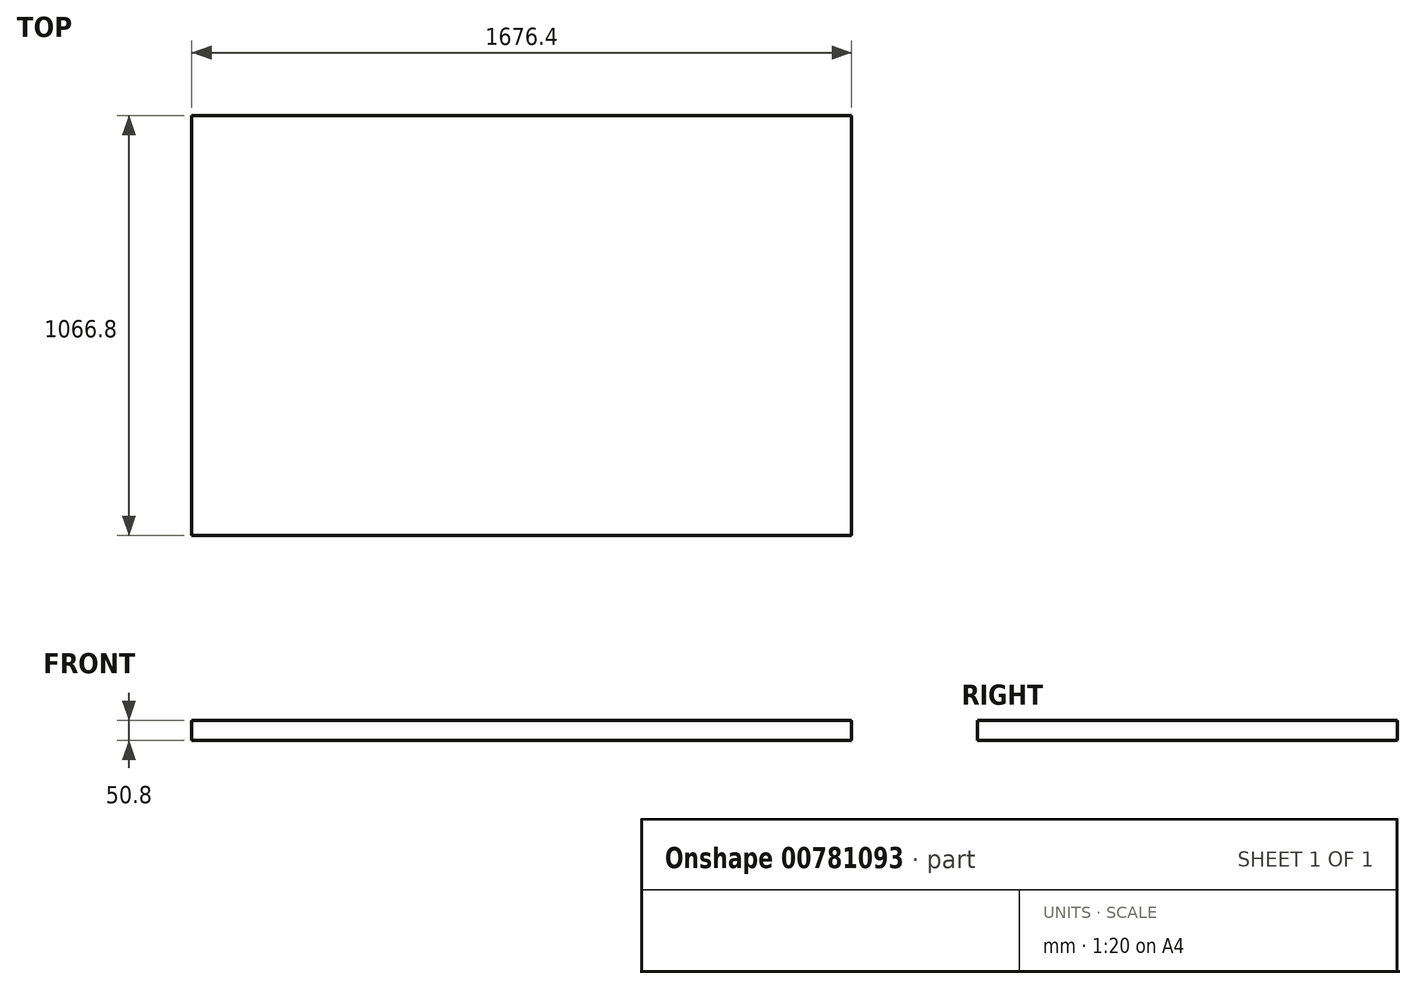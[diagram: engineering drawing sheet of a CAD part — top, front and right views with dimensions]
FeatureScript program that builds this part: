
annotation { "Feature Type Name" : "Feature", "Feature Type Description" : "" }
export const myFeature = defineFeature(function(context is Context, id is Id, definition is map)
    precondition{}
    {
        {
            var Q0;
            Q0=qCreatedBy(makeId("Top.planeOp"),FACE);
            var sketch = newSketch(context, id + "F0", { "sketchPlane" : qUnion([Q0])});
            skLineSegment(sketch, "E0.bottom", {"start": v(838.2, -533.4) * mm, "end": v(-838.2, -533.4) * mm});
            skLineSegment(sketch, "E0.top", {"start": v(838.2, 533.4) * mm, "end": v(-838.2, 533.4) * mm});
            skLineSegment(sketch, "E0.left", {"start": v(838.2, -533.4) * mm, "end": v(838.2, 533.4) * mm});
            skLineSegment(sketch, "E0.right", {"start": v(-838.2, -533.4) * mm, "end": v(-838.2, 533.4) * mm});
            skPoint(sketch, "E0.middle", {"position": v(0, 0) * mm});
            skSolve(sketch);
        }
        {
            var Q0;
            Q0=makeQuery(id+"F0.imprint","IMPRINT",FACE,{"disambiguationData":[TD([[makeQuery(id+"F0.imprint","IMPRINT",EDGE,{"derivedFrom":sQuery(id+"F0.wireOp",EDGE,"E0.bottom")}),-1.0]])]});
            extrude(context, id + "F1", {"entities" : qUnion([Q0]), "oppositeDirection" : true, "depth" : 50.8 * mm, "offsetDistance" : 25.4 * mm});
        }
    });
